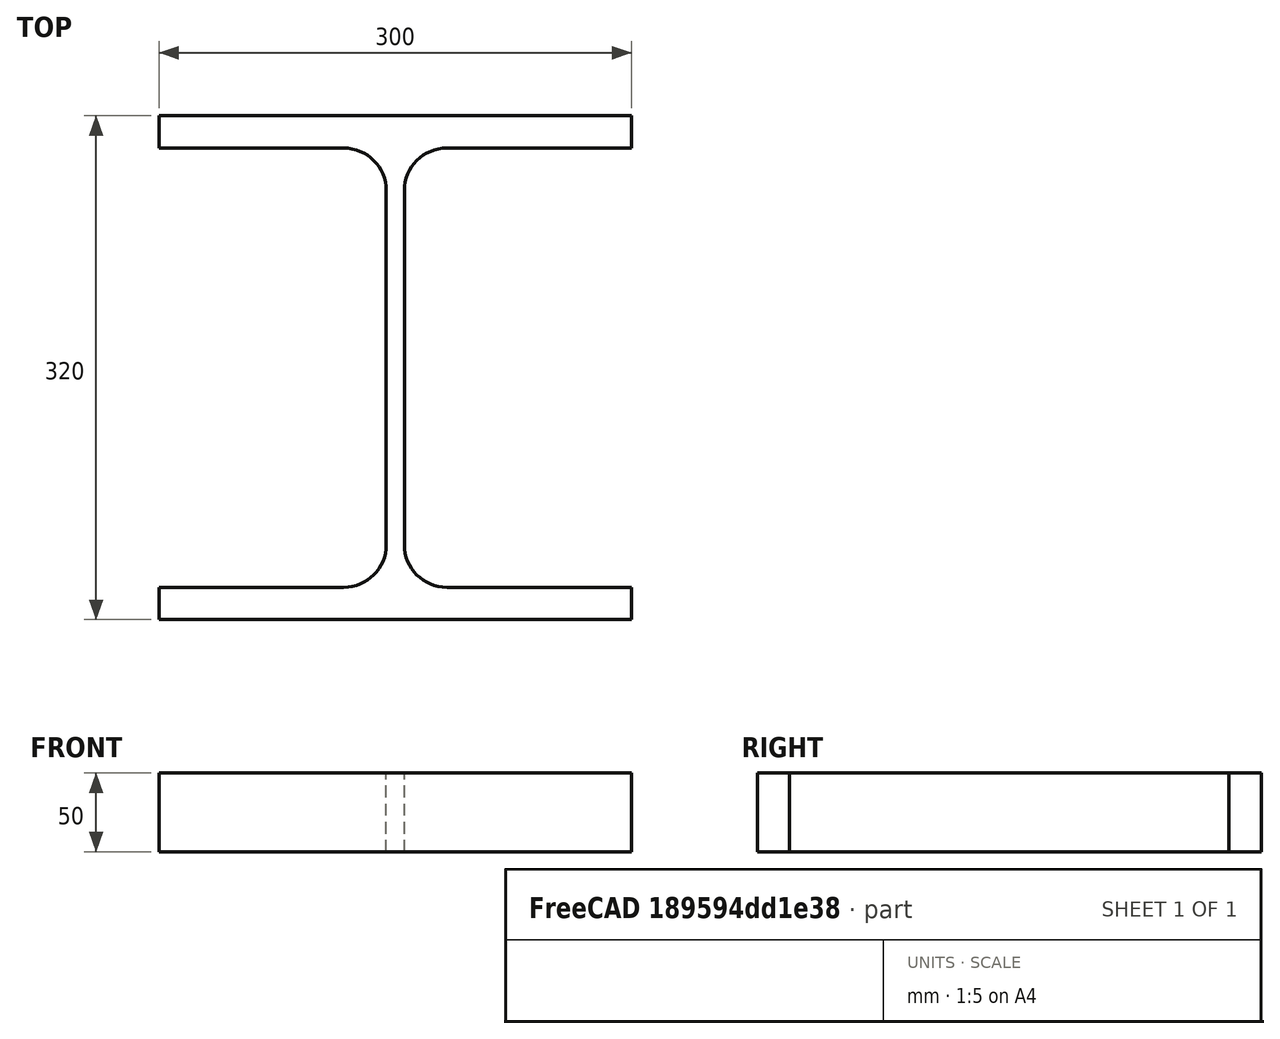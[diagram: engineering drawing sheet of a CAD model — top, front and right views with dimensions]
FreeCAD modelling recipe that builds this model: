
FCSTD DOCUMENT  (FreeCAD 0.15R4671 (Git))
Label: HE-B-Profile 320 DIN1025-2 S235JR
License: All rights reserved
LicenseURL: http://en.wikipedia.org/wiki/All_rights_reserved
objects: Sketcher::SketchObject×1, Part::Extrusion×1
note: 2 computed .brp shape members not serialized (recipe doc carries the construction recipe); baked Part::Feature solids carry a one-line shape summary decoded from their .brp

FEATURE [Sketcher::SketchObject] Sketch
  sketch-geometry (16):
    g0: LineSegment StartX=5.75 StartY=-112.5 StartZ=0 EndX=5.75 EndY=112.5 EndZ=0
    g1: LineSegment StartX=32.75 StartY=139.5 StartZ=0 EndX=150 EndY=139.5 EndZ=0
    g2: LineSegment StartX=150 StartY=139.5 StartZ=0 EndX=150 EndY=160 EndZ=0
    g3: LineSegment StartX=150 StartY=160 StartZ=0 EndX=-150 EndY=160 EndZ=0
    g4: LineSegment StartX=-150 StartY=160 StartZ=0 EndX=-150 EndY=139.5 EndZ=0
    g5: LineSegment StartX=-150 StartY=139.5 StartZ=0 EndX=-32.75 EndY=139.5 EndZ=0
    g6: LineSegment StartX=-5.75 StartY=112.5 StartZ=0 EndX=-5.75 EndY=-112.5 EndZ=0
    g7: LineSegment StartX=-32.75 StartY=-139.5 StartZ=0 EndX=-150 EndY=-139.5 EndZ=0
    g8: LineSegment StartX=-150 StartY=-139.5 StartZ=0 EndX=-150 EndY=-160 EndZ=0
    g9: LineSegment StartX=-150 StartY=-160 StartZ=0 EndX=150 EndY=-160 EndZ=0
    g10: LineSegment StartX=150 StartY=-160 StartZ=0 EndX=150 EndY=-139.5 EndZ=0
    g11: LineSegment StartX=150 StartY=-139.5 StartZ=0 EndX=32.75 EndY=-139.5 EndZ=0
    g12: ArcOfCircle CenterX=32.75 CenterY=112.5 CenterZ=0 NormalX=0 NormalY=0 NormalZ=1 Radius=27 StartAngle=1.5708 EndAngle=3.14159
    g13: ArcOfCircle CenterX=32.75 CenterY=-112.5 CenterZ=0 NormalX=0 NormalY=0 NormalZ=1 Radius=27 StartAngle=3.14159 EndAngle=4.71239
    g14: ArcOfCircle CenterX=-32.75 CenterY=112.5 CenterZ=0 NormalX=0 NormalY=0 NormalZ=1 Radius=27 StartAngle=0 EndAngle=1.5708
    g15: ArcOfCircle CenterX=-32.75 CenterY=-112.5 CenterZ=0 NormalX=0 NormalY=0 NormalZ=1 Radius=27 StartAngle=4.71239 EndAngle=6.28319
  constraints (42):
    c: Vertical(g0)
    c: Coincident(g2,g1)
    c: Vertical(g2)
    c: Coincident(g3,g2)
    c: Coincident(g4,g3)
    c: Vertical(g4)
    c: Coincident(g5,g4)
    c: Horizontal(g5)
    c: Vertical(g6)
    c: Horizontal(g7)
    c: Coincident(g8,g7)
    c: Vertical(g8)
    c: Coincident(g9,g8)
    c: Horizontal(g9)
    c: Coincident(g10,g9)
    c: Vertical(g10)
    c: Coincident(g11,g10)
    c: Horizontal(g11)
    c: Tangent(g1,g12) = 1.5708
    c: Tangent(g0,g12) = 1.5708
    c: Tangent(g0,g13) = 1.5708
    c: Tangent(g11,g13) = 1.5708
    c: Tangent(g5,g14) = 1.5708
    c: Tangent(g6,g14) = 1.5708
    c: Tangent(g6,g15) = 1.5708
    c: Tangent(g7,g15) = 1.5708
    c: Equal(g3,g9)
    c: Equal(g2,g4)
    c: Equal(g4,g8)
    c: Equal(g8,g10)
    c: Equal(g12,g14)
    c: Equal(g14,g15)
    c: Equal(g15,g13)
    c: Symmetric(g2,g3,g-2)
    c: Symmetric(g9,g8,g-2)
    c: Symmetric(g0,g6,g-2)
    c: Symmetric(g2,g9,g-1)
    c: DistanceY(g2,g9) = -320
    c: DistanceX(g3) = -300
    c: DistanceX(g0,g6) = -11.5
    c: DistanceY(g2) = 20.5
    c: Radius(g12) = 27
FEATURE [Part::Extrusion] Extrude  label="HE-B-Profile 320 DIN1025-2 S235JR"
  Base = -> Sketch
  Dir = (0,0,50)
  Solid = true
